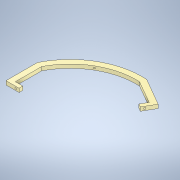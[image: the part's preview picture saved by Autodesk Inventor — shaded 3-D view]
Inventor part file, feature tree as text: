
AUTODESK INVENTOR PART (.ipt)
format: ipt  version: 2021 (Build 250183000, 183)  size: 167,424 bytes
history: native  units: in
note: dims shown in document units (in); Inventor stores cm internally (conversion verified against a paired STEP export)
features: sketch x4, other x3, hole x3, extrude x1
ambient origin geometry x8: Origin, YZ Plane, XZ Plane, XY Plane, X Axis, Y Axis, Z Axis, Center Point
bodies: Solid1 (feature_tree)
feature tree (11):
  extrude  "Extrusion1"  Depth=0.0315in
  other  "radial plane for hole1"
  sketch  "sketch hole 1"  dims[d5=0.0315in d6=0.0315in]
  other  "radial plane for hole2"
  hole  "Hole2"  [1 undecoded]
  hole  "Hole1"  [1 undecoded]
  other  "tangential plane for hole3"
  hole  "Hole3"  [1 undecoded]
  sketch  "Sketch1"  dims[d7=120.0deg d8=0.2in]
  sketch  "sketch hole 2"  dims[d9=0.2in d13=90.0deg]
  sketch  "Sketch6"  dims[d14=3.465in d15=0.3in d16=2.765in d17=90.0deg d19=0.3in d20=2.765in d21=0.7in d22=3.865in d23=3.565in d24=0.9252in d25=0.2in d26=0.0in d28=2.9398in d29=0.1in d30=2.9398in d31=0.1in d32=0.096in d33=0.75in d34=0.172in d35=0.25in d36=0.5635in d37=0.484in d38=0.8108in d39=0.096in d40=0.75in d41=0.172in d42=0.25in d43=0.5635in d44=0.484in d45=0.8108in d46=60.0deg d47=0.1in d48=0.0in d49=0.0849in d50=0.224in d51=0.225in d52=0.25in d53=0.5635in d54=0.349in d55=0.8108in]
note: 3 required parameter values undecoded (feature->parameter linkage not recoverable at this tier; creation-order binding heuristic only, values carry confidence <= 0.55)
